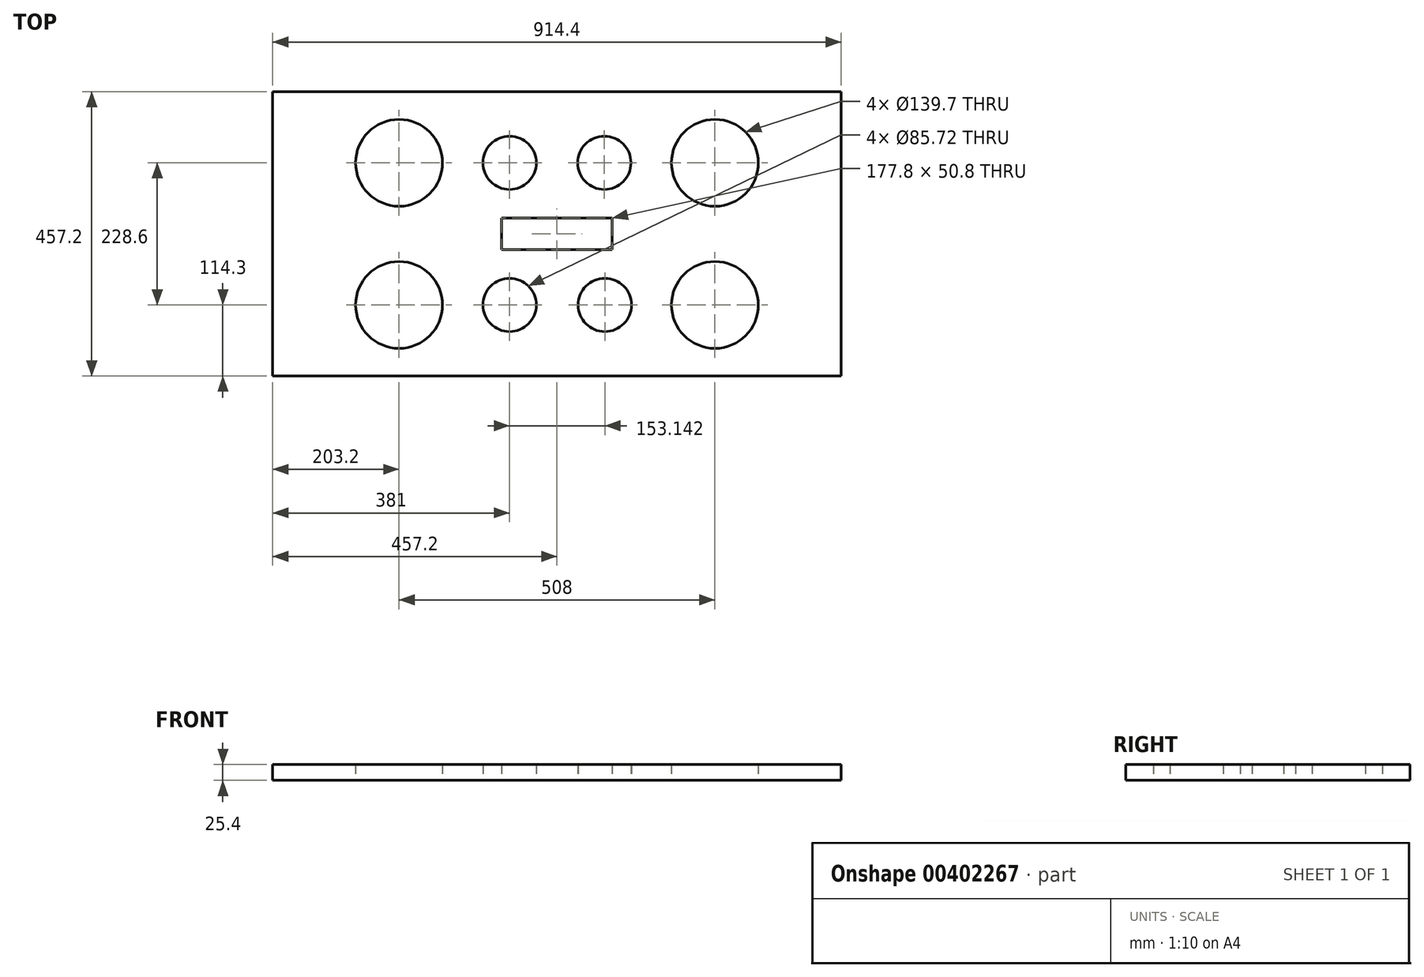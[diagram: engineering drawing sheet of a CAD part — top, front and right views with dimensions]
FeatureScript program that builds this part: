
annotation { "Feature Type Name" : "Feature", "Feature Type Description" : "" }
export const myFeature = defineFeature(function(context is Context, id is Id, definition is map)
    precondition{}
    {
        {
            var Q0;
            Q0=qCreatedBy(makeId("Top.planeOp"),FACE);
            var sketch = newSketch(context, id + "F0", { "sketchPlane" : qUnion([Q0])});
            skLineSegment(sketch, "E0.bottom", {"start": v(0, 0) * mm, "end": v(914.4, 0) * mm});
            skLineSegment(sketch, "E0.top", {"start": v(0, -457.2) * mm, "end": v(914.4, -457.2) * mm});
            skLineSegment(sketch, "E0.left", {"start": v(0, 0) * mm, "end": v(0, -457.2) * mm});
            skLineSegment(sketch, "E0.right", {"start": v(914.4, 0) * mm, "end": v(914.4, -457.2) * mm});
            skCircle(sketch, "E1", {"center": v(203.2, -114.3) * mm, "radius": 69.85 * mm});
            skCircle(sketch, "E2", {"center": v(711.2, -114.3) * mm, "radius": 69.85 * mm});
            skCircle(sketch, "E3", {"center": v(203.2, -342.9) * mm, "radius": 69.85 * mm});
            skCircle(sketch, "E4", {"center": v(711.2, -342.9) * mm, "radius": 69.85 * mm});
            skCircle(sketch, "E5", {"center": v(381, -114.3) * mm, "radius": 42.86 * mm});
            skCircle(sketch, "E6", {"center": v(533.38, -114.3) * mm, "radius": 42.86 * mm});
            skCircle(sketch, "E7", {"center": v(381, -342.9) * mm, "radius": 42.86 * mm});
            skCircle(sketch, "E8", {"center": v(534.14, -342.9) * mm, "radius": 42.86 * mm});
            skLineSegment(sketch, "E9.bottom", {"start": v(546.1, -254) * mm, "end": v(368.3, -254) * mm});
            skLineSegment(sketch, "E9.top", {"start": v(546.1, -203.2) * mm, "end": v(368.3, -203.2) * mm});
            skLineSegment(sketch, "E9.left", {"start": v(546.1, -254) * mm, "end": v(546.1, -203.2) * mm});
            skLineSegment(sketch, "E9.right", {"start": v(368.3, -254) * mm, "end": v(368.3, -203.2) * mm});
            skSolve(sketch);
        }
        {
            var Q0;
            Q0=makeQuery(id+"F0.imprint","IMPRINT",FACE,{"disambiguationData":[TD([[makeQuery(id+"F0.imprint","IMPRINT",EDGE,{"derivedFrom":sQuery(id+"F0.wireOp",EDGE,"E0.bottom")}),-1.0]])]});
            extrude(context, id + "F1", {"entities" : qUnion([Q0]), "depth" : 19.05 * mm});
        }
        {
            var Q0;
            Q0=makeQuery(id+"FkSZoEzsc55wibZ_1.boolean.opBoolean","SPLIT",FACE,{"disambiguationData":[TD([makeQuery(id+"FkSZoEzsc55wibZ_1.opExtrude","SWEPT_FACE",FACE,{"disambiguationData":[OSD([sQuery(id+"FUJ6yJvK5KAznJR_1.wireOp",EDGE,"FcbFxkr0-WuCM-DDUM-Nblf-k06435lk3dIT")])]})])],"derivedFrom":makeQuery(id+"F1.opExtrude","CAP_FACE",FACE,{"disambiguationData":[OSD([sQuery(id+"F0.wireOp",EDGE,"E0.bottom"),sQuery(id+"F0.wireOp",EDGE,"E0.top"),sQuery(id+"F0.wireOp",EDGE,"E0.left"),sQuery(id+"F0.wireOp",EDGE,"E0.right"),sQuery(id+"F0.wireOp",EDGE,"czYkPL4u-2bsI-opME-QwsZ-lVEJJLye0A5B"),sQuery(id+"F0.wireOp",EDGE,"E1"),sQuery(id+"F0.wireOp",EDGE,"E2"),sQuery(id+"F0.wireOp",EDGE,"E3"),sQuery(id+"F0.wireOp",EDGE,"E4"),sQuery(id+"F0.wireOp",EDGE,"E5"),sQuery(id+"F0.wireOp",EDGE,"E6"),sQuery(id+"F0.wireOp",EDGE,"E7"),sQuery(id+"F0.wireOp",EDGE,"E8"),sQuery(id+"F0.wireOp",EDGE,"E9.bottom"),sQuery(id+"F0.wireOp",EDGE,"E9.top"),sQuery(id+"F0.wireOp",EDGE,"E9.left"),sQuery(id+"F0.wireOp",EDGE,"E9.right")])],"isStart":true})});
            extrude(context, id + "F2", {"entities" : qUnion([Q0]), "operationType" : NewBodyOperationType.ADD, "oppositeDirection" : true, "depth" : 25.4 * mm});
        }
    });
